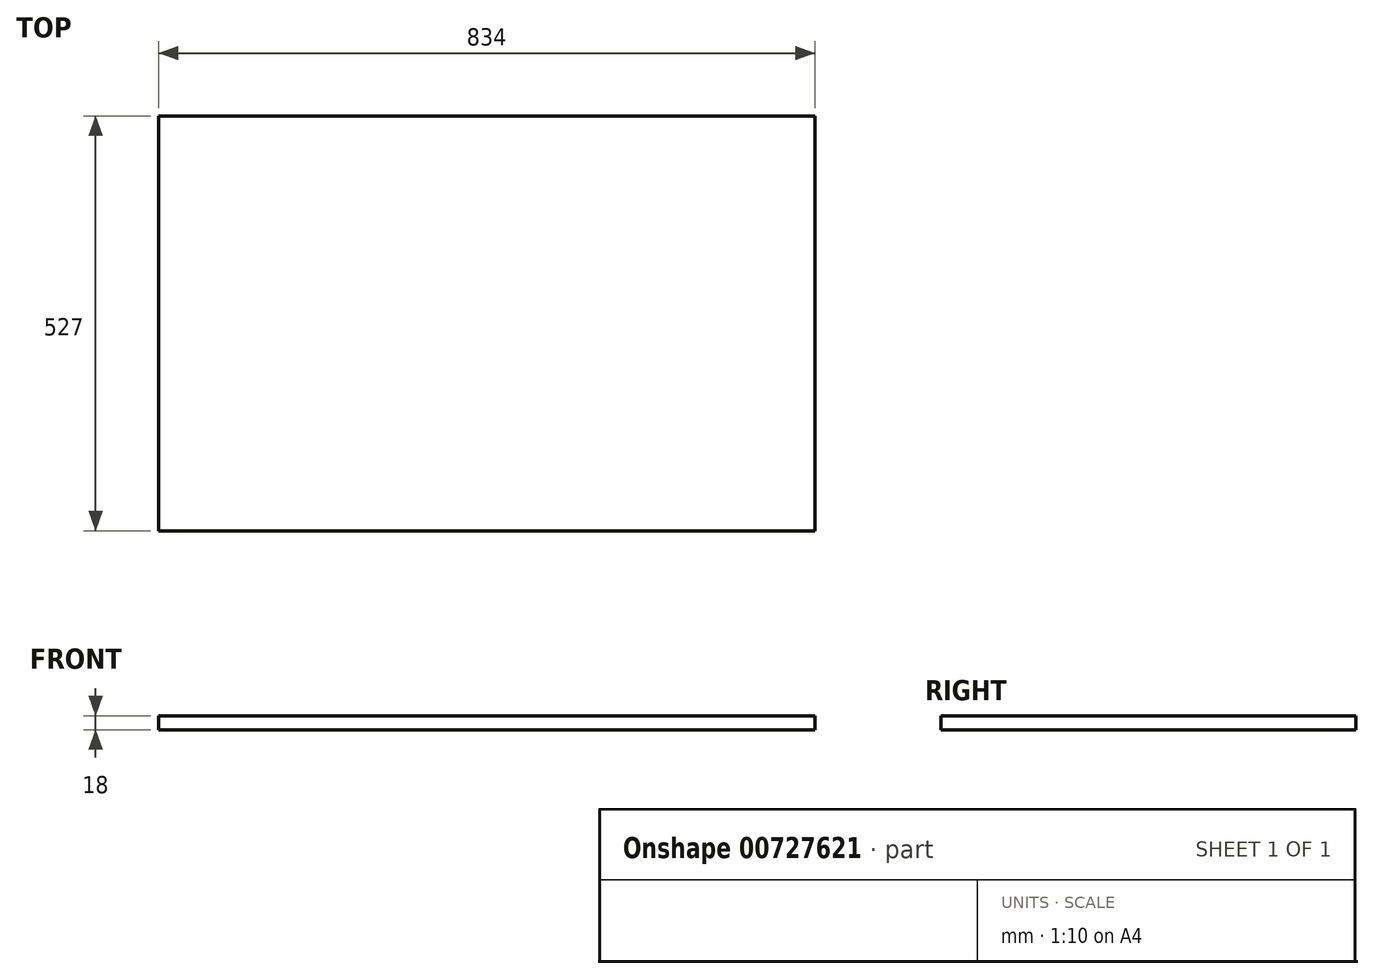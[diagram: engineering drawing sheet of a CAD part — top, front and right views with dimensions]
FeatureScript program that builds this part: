
annotation { "Feature Type Name" : "Feature", "Feature Type Description" : "" }
export const myFeature = defineFeature(function(context is Context, id is Id, definition is map)
    precondition{}
    {
        {
            var Q0;
            Q0=qCreatedBy(makeId("Top.planeOp"),FACE);
            var sketch = newSketch(context, id + "F0", { "sketchPlane" : qUnion([Q0])});
            skLineSegment(sketch, "E0.bottom", {"start": v(-417, 263.5) * mm, "end": v(417, 263.5) * mm});
            skLineSegment(sketch, "E0.top", {"start": v(-417, -263.5) * mm, "end": v(417, -263.5) * mm});
            skLineSegment(sketch, "E0.left", {"start": v(-417, 263.5) * mm, "end": v(-417, -263.5) * mm});
            skLineSegment(sketch, "E0.right", {"start": v(417, 263.5) * mm, "end": v(417, -263.5) * mm});
            skLineSegment(sketch, "E1", {"start": v(417, 263.5) * mm, "end": v(-417, -263.5) * mm, "construction": true});
            skSolve(sketch);
        }
        {
            var Q0;
            Q0 = qSketchRegion(id + "F0", true);
            extrude(context, id + "F1", {"entities" : qUnion([Q0]), "depth" : 18 * mm, "offsetDistance" : 25 * mm});
        }
    });
